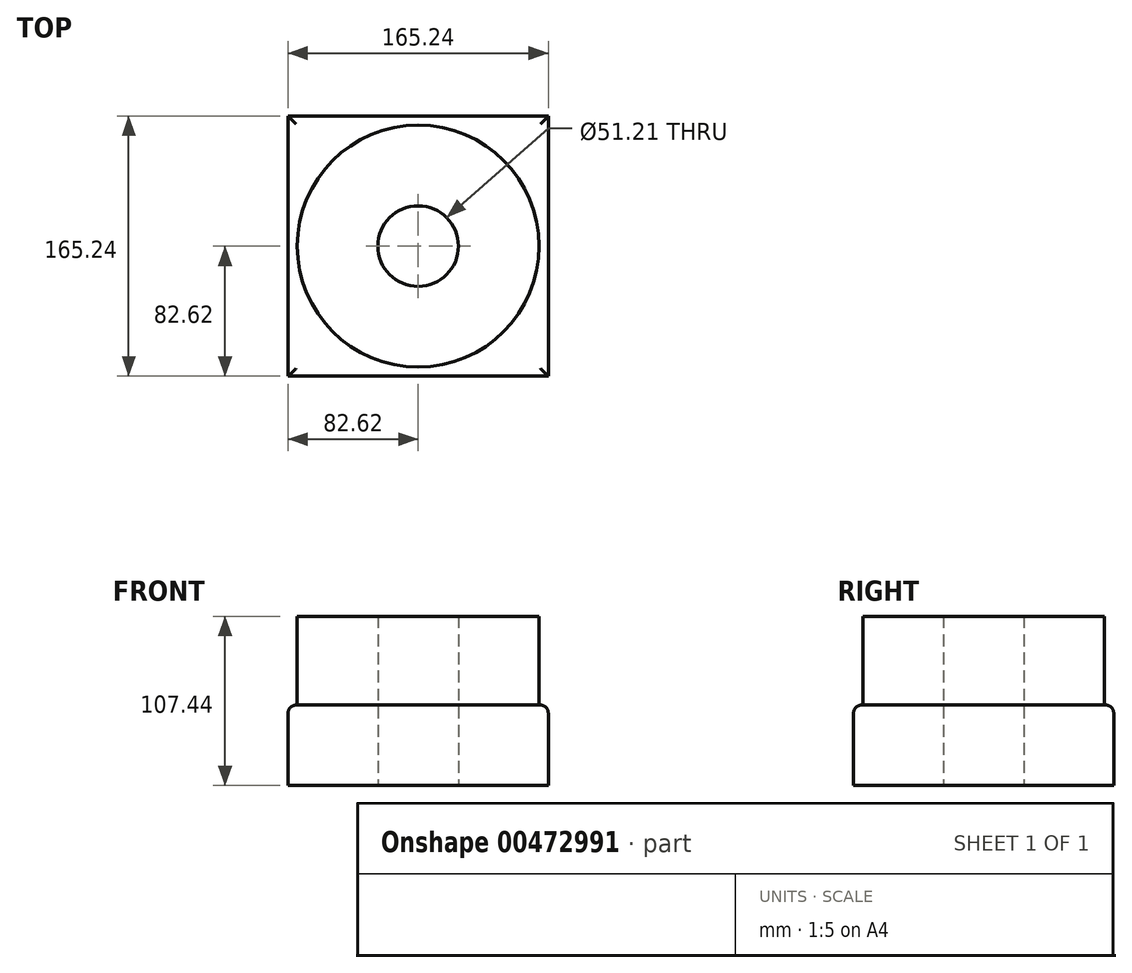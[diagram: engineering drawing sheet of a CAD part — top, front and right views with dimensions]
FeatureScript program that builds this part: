
annotation { "Feature Type Name" : "Feature", "Feature Type Description" : "" }
export const myFeature = defineFeature(function(context is Context, id is Id, definition is map)
    precondition{}
    {
        {
            var Q0;
            Q0=qCreatedBy(makeId("Top.planeOp"),FACE);
            var sketch = newSketch(context, id + "F0", { "sketchPlane" : qUnion([Q0])});
            skLineSegment(sketch, "E0.bottom", {"start": v(-82.62, 82.62) * mm, "end": v(82.62, 82.62) * mm});
            skLineSegment(sketch, "E0.top", {"start": v(-82.62, -82.62) * mm, "end": v(82.62, -82.62) * mm});
            skLineSegment(sketch, "E0.left", {"start": v(-82.62, 82.62) * mm, "end": v(-82.62, -82.62) * mm});
            skLineSegment(sketch, "E0.right", {"start": v(82.62, 82.62) * mm, "end": v(82.62, -82.62) * mm});
            skCircle(sketch, "E1", {"center": v(0, 0) * mm, "radius": 82.62 * mm, "construction": true});
            skCircle(sketch, "E2", {"center": v(0, 0) * mm, "radius": 25.6 * mm});
            skSolve(sketch);
        }
        {
            var Q0;
            Q0=makeQuery(id+"F0.imprint","IMPRINT",FACE,{"disambiguationData":[TD([[makeQuery(id+"F0.imprint","IMPRINT",EDGE,{"derivedFrom":sQuery(id+"F0.wireOp",EDGE,"E0.bottom")}),-1.0]])]});
            var sketch = newSketch(context, id + "F1", { "sketchPlane" : qUnion([Q0])});
            skCircle(sketch, "E3", {"center": v(0, 0) * mm, "radius": 76.8 * mm});
            skCircle(sketch, "E4", {"center": v(51.2, 0) * mm, "radius": 25.6 * mm, "construction": true});
            skSolve(sketch);
        }
        {
            var Q0;
            Q0 = qSketchRegion(id + "F0", true);
            extrude(context, id + "F2", {"entities" : qUnion([Q0]), "depth" : 51.05 * mm});
        }
        {
            var Q0;
            Q0=makeQuery(id+"F2.opExtrude","CAP_EDGE",EDGE,{"disambiguationData":[OSD([sQuery(id+"F0.wireOp",EDGE,"E0.left")])],"isStart":false});
            var Q1;
            Q1=makeQuery(id+"F2.opExtrude","CAP_EDGE",EDGE,{"disambiguationData":[OSD([sQuery(id+"F0.wireOp",EDGE,"E0.top")])],"isStart":false});
            var Q2;
            Q2=makeQuery(id+"F2.opExtrude","CAP_EDGE",EDGE,{"disambiguationData":[OSD([sQuery(id+"F0.wireOp",EDGE,"E0.right")])],"isStart":false});
            var Q3;
            Q3=makeQuery(id+"F2.opExtrude","CAP_EDGE",EDGE,{"disambiguationData":[OSD([sQuery(id+"F0.wireOp",EDGE,"E0.bottom")])],"isStart":false});
            fillet(context, id + "F3", {"entities" : qUnion([Q0, Q1, Q2, Q3]), "radius" : 5.08 * mm, "tangentPropagation" : true, "allowEdgeOverflow" : false});
        }
        {
            var Q0;
            Q0=makeQuery(id+"F1.imprint","IMPRINT",FACE,{"disambiguationData":[TD([[makeQuery(id+"F1.imprint","IMPRINT",EDGE,{"derivedFrom":sQuery(id+"F1.wireOp",EDGE,"E3")}),1.0]])]});
            extrude(context, id + "F4", {"entities" : qUnion([Q0]), "operationType" : NewBodyOperationType.ADD, "depth" : 107.44 * mm});
        }
    });
